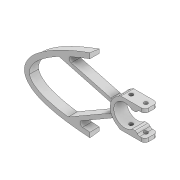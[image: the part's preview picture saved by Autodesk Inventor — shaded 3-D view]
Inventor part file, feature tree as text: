
AUTODESK INVENTOR PART (.ipt)
format: ipt  version: 2022 (Build 260153000, 153)  size: 567,296 bytes
history: native  units: mm
features: extrude x6, sketch x6, projected_geometry x3, fillet x2, shell x1, thicken_offset x1, chamfer x1
ambient origin geometry x8: Origin, YZ Plane, XZ Plane, XY Plane, X Axis, Y Axis, Z Axis, Center Point
bodies: Solid1 (feature_tree)
feature tree (20):
  extrude  "Extrusion1"  Depth=2.0mm
  shell  "Shell1"  Thickness=55.0mm
  extrude  "Extrusion9"  Depth=12.0mm
  fillet  "Fillet2"  Radius=2.0mm
  extrude  "Extrusion10"  Depth=11.0mm
  extrude  "Extrusion12"  TaperAngle=30.0deg  [1 undecoded]
  thicken_offset  "Thicken1"
  chamfer  "Chamfer1"  Distance=2.0mm
  extrude  "Extrusion13"  Depth=2.0mm
  extrude  "Extrusion14"  Depth=1.5mm
  fillet  "Fillet3"  Radius=1.5mm
  sketch  "Sketch3"  dims[d0=5.0mm d1=0.0mm d2=2.0mm d68=55.0mm]
  sketch  "Sketch25"  dims[d69=8.05mm d70=12.0mm d71=2.0mm]
  projected_geometry  "Projected Loop13"
  sketch  "Sketch26"  dims[d72=11.0mm d73=11.0mm]
  sketch  "Sketch28"  dims[d74=15.0deg d75=30.0deg]
  sketch  "Sketch30"  dims[d76=2.0mm]
  projected_geometry  "Projected Loop15"
  sketch  "Sketch31"  dims[d77=1.0mm d79=2.0mm d80=1.0mm d81=1.5mm d82=1.5mm d83=5.0mm d84=0.0mm d85=3.0mm d86=3.0mm d87=1.5mm d88=35.0mm d89=35.0mm d90=100.0mm d91=0.0mm d98=2.1mm d99=2.5mm d100=2.1mm d101=3.0mm d102=30.0mm d103=0.0mm d104=0.7mm d105=0.7mm d106=5.0mm d107=0.65mm d108=45.0deg d109=1.0mm d110=0.0mm d111=1.0mm d112=0.0mm d113=2.0mm]
  projected_geometry  "Projected Loop16"
note: 1 required parameter value undecoded (feature->parameter linkage not recoverable at this tier; creation-order binding heuristic only, values carry confidence <= 0.55)
